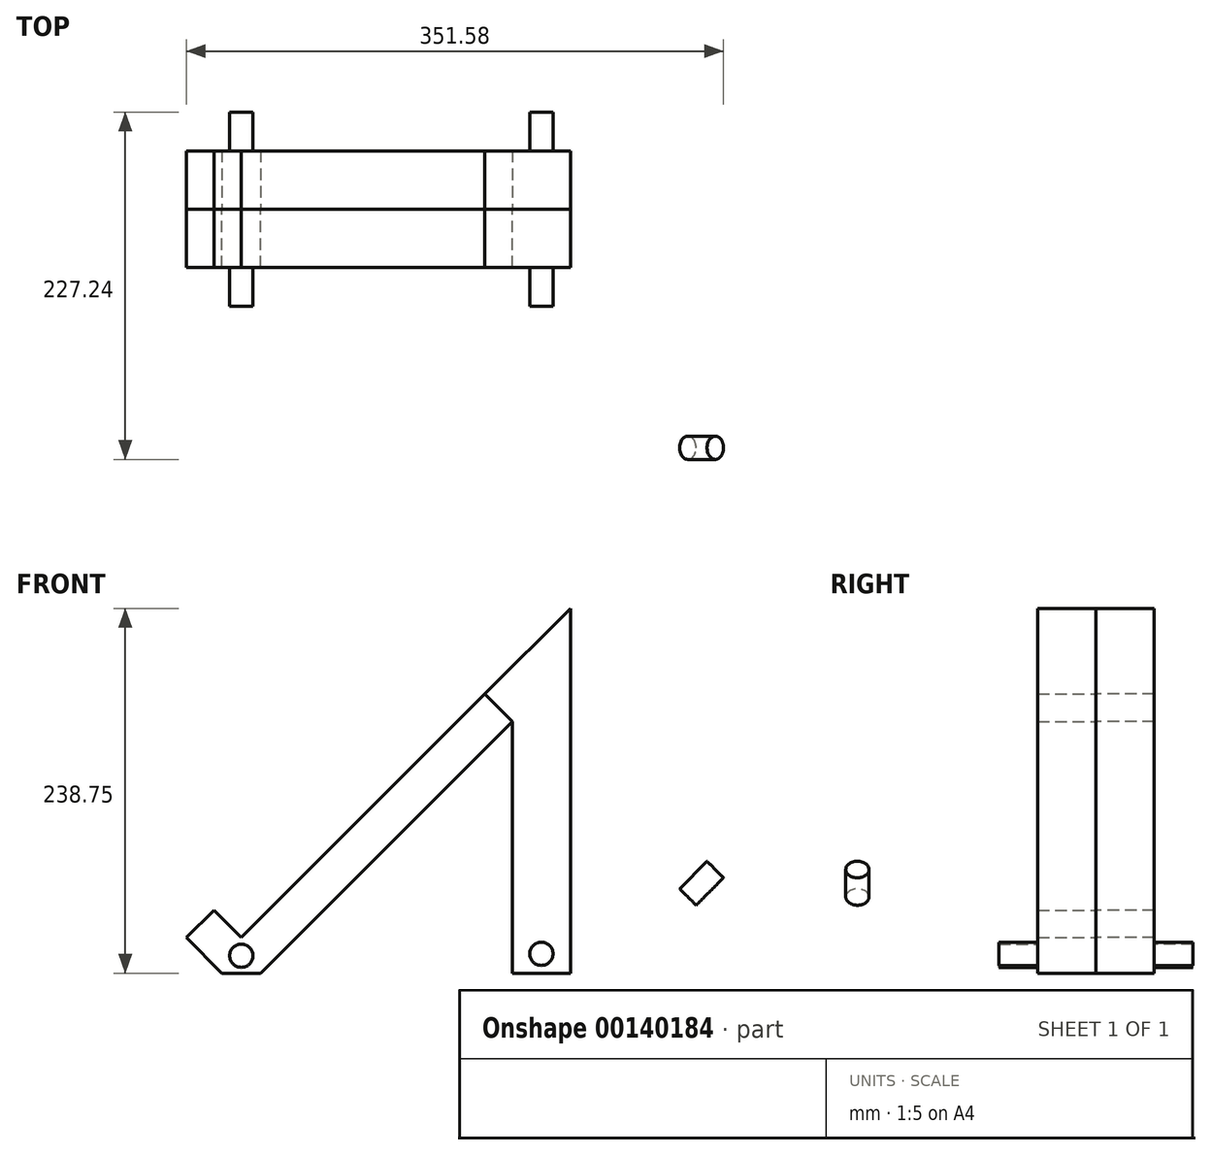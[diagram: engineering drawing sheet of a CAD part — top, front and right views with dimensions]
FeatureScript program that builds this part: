
annotation { "Feature Type Name" : "Feature", "Feature Type Description" : "" }
export const myFeature = defineFeature(function(context is Context, id is Id, definition is map)
    precondition{}
    {
        {
            var Q0;
            Q0=qCreatedBy(makeId("Front.planeOp"),FACE);
            var sketch = newSketch(context, id + "F0", { "sketchPlane" : qUnion([Q0])});
            skLineSegment(sketch, "E0", {"start": v(0, 0) * mm, "end": v(0, 238.75) * mm});
            skLineSegment(sketch, "E1", {"start": v(0, 238.75) * mm, "end": v(-215.53, 23.22) * mm});
            skLineSegment(sketch, "E2", {"start": v(-215.53, 23.22) * mm, "end": v(-233.49, 41.18) * mm});
            skLineSegment(sketch, "E3", {"start": v(-233.49, 41.18) * mm, "end": v(-251.45, 23.22) * mm});
            skLineSegment(sketch, "E4", {"start": v(-251.45, 23.22) * mm, "end": v(-228.23, 0) * mm});
            skLineSegment(sketch, "E5", {"start": v(-228.23, 0) * mm, "end": v(-202.83, 0) * mm});
            skLineSegment(sketch, "E6", {"start": v(-202.83, 0) * mm, "end": v(-38.1, 164.73) * mm});
            skLineSegment(sketch, "E7", {"start": v(-38.1, 164.73) * mm, "end": v(-38.1, 0) * mm});
            skLineSegment(sketch, "E8", {"start": v(-38.1, 0) * mm, "end": v(0, 0) * mm});
            skLineSegment(sketch, "E9", {"start": v(-38.1, 164.73) * mm, "end": v(-56.06, 182.69) * mm});
            skSolve(sketch);
        }
        {
            var Q0;
            {var subQ0=sQuery(id+"F0.wireOp",EDGE,"E2");Q0=makeQuery(id+"F0.imprint","IMPRINT",FACE,{"disambiguationData":[TD([[makeQuery(id+"F0.imprint","IMPRINT",EDGE,{"derivedFrom":subQ0}),1.0]])]});}
            extrude(context, id + "F1", {"entities" : qUnion([Q0]), "depth" : 38.1 * mm});
        }
        {
            var Q0;
            {var subQ1=sQuery(id+"F0.wireOp",EDGE,"E0");Q0=makeQuery(id+"F0.imprint","IMPRINT",FACE,{"disambiguationData":[TD([[makeQuery(id+"F0.imprint","IMPRINT",EDGE,{"derivedFrom":subQ1}),1.0]])]});}
            extrude(context, id + "F2", {"entities" : qUnion([Q0]), "depth" : 38.1 * mm});
        }
        {
            var Q0;
            Q0=makeQuery(id+"F1.opExtrude","SWEPT_FACE",FACE,{"disambiguationData":[OSD([sQuery(id+"F0.wireOp",EDGE,"E9")])]});
            var sketch = newSketch(context, id + "F3", { "sketchPlane" : qUnion([Q0])});
            skCircle(sketch, "E10", {"center": v(-156.12, -19.05) * mm, "radius": 7.62 * mm});
            skPoint(sketch, "E10.centerSnap0", {"position": v(-168.82, -19.05) * mm});
            skPoint(sketch, "E10.centerSnap1", {"position": v(-156.12, 0) * mm});
            skSolve(sketch);
        }
        {
            var Q0;
            Q0 = qSketchRegion(id + "F3", true);
            extrude(context, id + "F4", {"entities" : qUnion([Q0]), "operationType" : NewBodyOperationType.ADD, "depth" : 25.4 * mm});
        }
        {
            var Q0;
            Q0=makeQuery(id+"F2.opExtrude","SWEPT_FACE",FACE,{"disambiguationData":[OSD([sQuery(id+"F0.wireOp",EDGE,"E9")])]});
            var sketch = newSketch(context, id + "F5", { "sketchPlane" : qUnion([Q0])});
            skCircle(sketch, "E11", {"center": v(-156.12, 19.05) * mm, "radius": 7.75 * mm});
            skPoint(sketch, "E11.centerSnap0", {"position": v(-156.12, 38.1) * mm});
            skPoint(sketch, "E11.centerSnap1", {"position": v(-168.82, 19.05) * mm});
            skSolve(sketch);
        }
        {
            var Q0;
            Q0=makeQuery(id+"F5.imprint","IMPRINT",FACE,{"disambiguationData":[TD([[makeQuery(id+"F5.imprint","IMPRINT",EDGE,{"derivedFrom":sQuery(id+"F5.wireOp",EDGE,"E11")}),1.0]])]});
            extrude(context, id + "F6", {"entities" : qUnion([Q0]), "operationType" : NewBodyOperationType.REMOVE, "oppositeDirection" : true, "depth" : 27.94 * mm});
        }
        {
            var Q0;
            Q0=makeQuery(id+"F1.opExtrude","CAP_FACE",FACE,{"disambiguationData":[OSD([sQuery(id+"F0.wireOp",EDGE,"E1"),sQuery(id+"F0.wireOp",EDGE,"E2"),sQuery(id+"F0.wireOp",EDGE,"E3"),sQuery(id+"F0.wireOp",EDGE,"E4"),sQuery(id+"F0.wireOp",EDGE,"E5"),sQuery(id+"F0.wireOp",EDGE,"E6"),sQuery(id+"F0.wireOp",EDGE,"E9")])],"isStart":false});
            var sketch = newSketch(context, id + "F7", { "sketchPlane" : qUnion([Q0])});
            skCircle(sketch, "E12", {"center": v(-215.53, 11.43) * mm, "radius": 7.62 * mm});
            skPoint(sketch, "E12.centerSnap0", {"position": v(-215.53, 0) * mm});
            skSolve(sketch);
        }
        {
            var Q0;
            Q0 = qSketchRegion(id + "F7", true);
            extrude(context, id + "F8", {"entities" : qUnion([Q0]), "operationType" : NewBodyOperationType.ADD, "depth" : 25.4 * mm});
        }
        {
            var Q0;
            Q0=makeQuery(id+"F2.opExtrude","CAP_FACE",FACE,{"disambiguationData":[OSD([sQuery(id+"F0.wireOp",EDGE,"E0"),sQuery(id+"F0.wireOp",EDGE,"E1"),sQuery(id+"F0.wireOp",EDGE,"E7"),sQuery(id+"F0.wireOp",EDGE,"E8"),sQuery(id+"F0.wireOp",EDGE,"E9")])],"isStart":false});
            var sketch = newSketch(context, id + "F9", { "sketchPlane" : qUnion([Q0])});
            skCircle(sketch, "E13", {"center": v(-19.05, 12.7) * mm, "radius": 7.62 * mm});
            skPoint(sketch, "E13.centerSnap0", {"position": v(-19.05, 0) * mm});
            skSolve(sketch);
        }
        {
            var Q0;
            Q0 = qSketchRegion(id + "F9", true);
            extrude(context, id + "F10", {"entities" : qUnion([Q0]), "operationType" : NewBodyOperationType.ADD, "depth" : 25.4 * mm});
        }
        {
            var Q0;
            Q0=makeQuery(id+"F2.opExtrude","SWEPT_BODY",BODY,{"disambiguationData":[OSD([sQuery(id+"F0.wireOp",EDGE,"E0"),sQuery(id+"F0.wireOp",EDGE,"E1"),sQuery(id+"F0.wireOp",EDGE,"E7"),sQuery(id+"F0.wireOp",EDGE,"E8"),sQuery(id+"F0.wireOp",EDGE,"E9")])]});
            var Q1;
            Q1=makeQuery(id+"F1.opExtrude","SWEPT_BODY",BODY,{"disambiguationData":[OSD([sQuery(id+"F0.wireOp",EDGE,"E1"),sQuery(id+"F0.wireOp",EDGE,"E2"),sQuery(id+"F0.wireOp",EDGE,"E3"),sQuery(id+"F0.wireOp",EDGE,"E4"),sQuery(id+"F0.wireOp",EDGE,"E5"),sQuery(id+"F0.wireOp",EDGE,"E6"),sQuery(id+"F0.wireOp",EDGE,"E9")])]});
            var Q2;
            Q2=qCreatedBy(makeId("Front.planeOp"),FACE);
            mirror(context, id + "F11", {"entities" : qUnion([Q0, Q1]), "mirrorPlane" : qUnion([Q2])});
        }
    });
